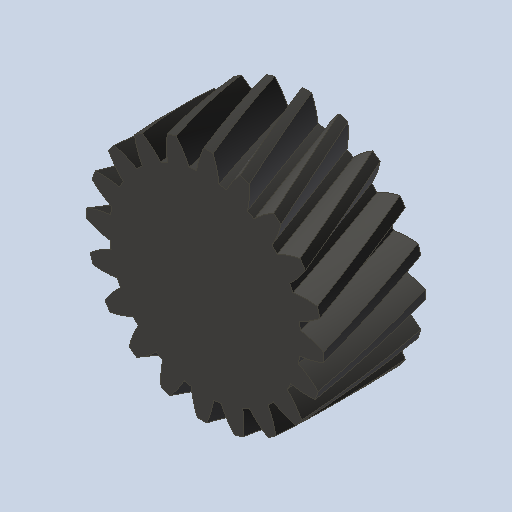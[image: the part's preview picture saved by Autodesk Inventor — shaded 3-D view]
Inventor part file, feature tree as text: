
AUTODESK INVENTOR PART (.ipt)
format: ipt  version: 2023 (Build 270158000, 158)  size: 380,416 bytes
history: native  units: mm (DEFAULTED — no unit token found)
features: plane x3, other x3, sketch x2, extrude x1
ambient origin geometry x8: Origin, YZ Plane, XZ Plane, XY Plane, X Axis, Y Axis, Z Axis, Center Point
bodies: Solid1 (feature_tree)
feature tree (9):
  extrude  "Extrusion1"  Depth=15.0mm TaperAngle=0.0deg
  plane  "Work Plane2"
  plane  "Work Plane8"
  plane  "Work Plane9"
  other  "Spur Gear"
  sketch  "Sketch1"  dims[d0=34.921665mm d1=15.0mm d2=0.0mm]
  sketch  "Sketch2"  dims[d3=31.925333mm d4=10.0mm d5=0.0mm d16=101.6mm d17=0.0mm d34=1.570796mm d39=0.0mm d41=0.0mm d43=101.6mm d46=101.6mm d47=0.0mm d48=0.0mm]
  other  "Srf1"
  other  "Pitch Diameter"
